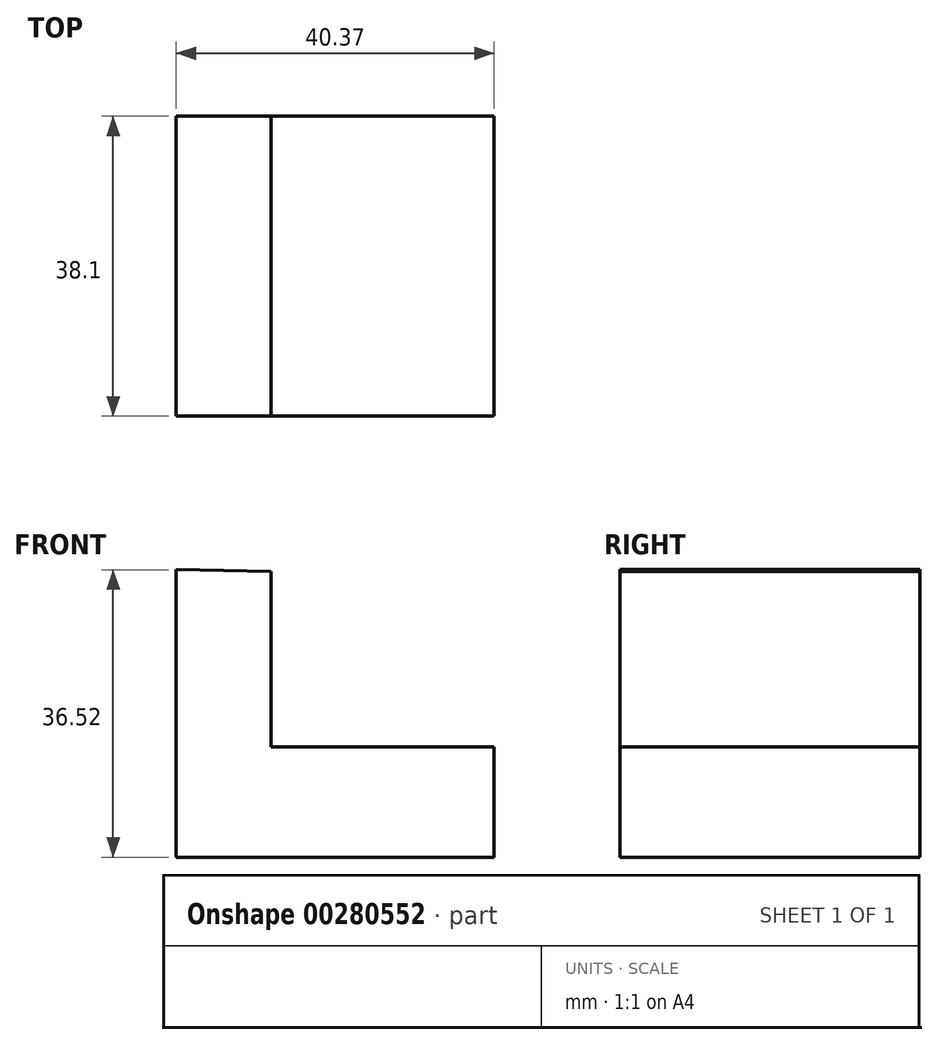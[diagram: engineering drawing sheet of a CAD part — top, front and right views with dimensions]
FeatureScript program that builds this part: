
annotation { "Feature Type Name" : "Feature", "Feature Type Description" : "" }
export const myFeature = defineFeature(function(context is Context, id is Id, definition is map)
    precondition{}
    {
        {
            var Q0;
            Q0=qCreatedBy(makeId("Front.planeOp"),FACE);
            var sketch = newSketch(context, id + "F0", { "sketchPlane" : qUnion([Q0])});
            skLineSegment(sketch, "E0", {"start": v(-64.06, 36.52) * mm, "end": v(-64.06, 0) * mm});
            skLineSegment(sketch, "E1", {"start": v(-64.06, 0) * mm, "end": v(-23.69, 0) * mm});
            skLineSegment(sketch, "E2", {"start": v(-23.69, 0) * mm, "end": v(-23.69, 14.03) * mm});
            skLineSegment(sketch, "E3", {"start": v(-23.69, 14.03) * mm, "end": v(-52.01, 14.03) * mm});
            skLineSegment(sketch, "E4", {"start": v(-52.01, 14.03) * mm, "end": v(-52.01, 36.32) * mm});
            skLineSegment(sketch, "E5", {"start": v(-52.01, 36.32) * mm, "end": v(-64.06, 36.52) * mm});
            skSolve(sketch);
        }
        {
            var Q0;
            Q0=makeQuery(id+"F0.imprint","IMPRINT",FACE,{"disambiguationData":[TD([[makeQuery(id+"F0.imprint","IMPRINT",EDGE,{"derivedFrom":sQuery(id+"F0.wireOp",EDGE,"E0")}),1.0]])]});
            extrude(context, id + "F1", {"entities" : qUnion([Q0]), "depth" : 38.1 * mm});
        }
    });
